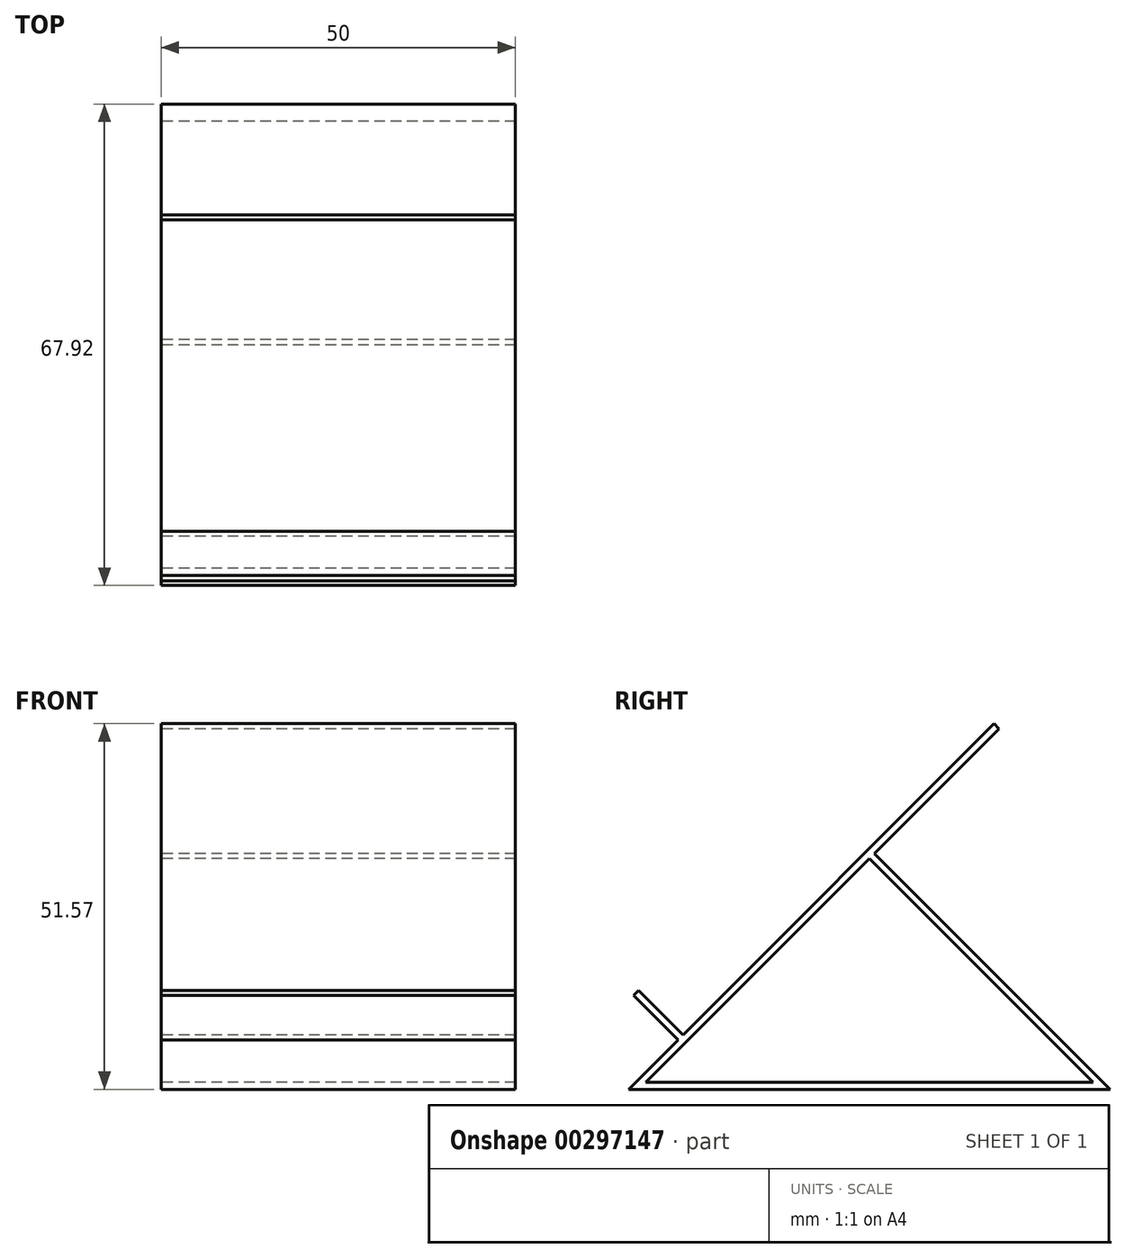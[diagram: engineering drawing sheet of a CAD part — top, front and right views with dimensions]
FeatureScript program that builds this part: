
annotation { "Feature Type Name" : "Feature", "Feature Type Description" : "" }
export const myFeature = defineFeature(function(context is Context, id is Id, definition is map)
    precondition{}
    {
        {
            var Q0;
            Q0=qCreatedBy(makeId("Right.planeOp"),FACE);
            var sketch = newSketch(context, id + "F0", { "sketchPlane" : qUnion([Q0])});
            skLineSegment(sketch, "E0", {"start": v(-32.75, 0) * mm, "end": v(32.75, 0) * mm, "construction": true});
            skLineSegment(sketch, "E1", {"start": v(-32.75, 0) * mm, "end": v(17.97, 50.72) * mm, "construction": true});
            skLineSegment(sketch, "E2", {"start": v(32.75, 0) * mm, "end": v(0, 32.75) * mm, "construction": true});
            skLineSegment(sketch, "E3.0", {"start": v(-33.96, -0.5) * mm, "end": v(-27, 6.46) * mm});
            skLineSegment(sketch, "E4.0", {"start": v(-31.54, 0.5) * mm, "end": v(0, 32.04) * mm});
            skLineSegment(sketch, "E5.0", {"start": v(33.96, -0.5) * mm, "end": v(0.7, 32.75) * mm});
            skLineSegment(sketch, "E6.0", {"start": v(-31.54, 0.5) * mm, "end": v(31.54, 0.5) * mm});
            skLineSegment(sketch, "E7.0", {"start": v(31.54, 0.5) * mm, "end": v(0, 32.04) * mm});
            skLineSegment(sketch, "E8.0", {"start": v(-33.96, -0.5) * mm, "end": v(33.96, -0.5) * mm});
            skLineSegment(sketch, "E9", {"start": v(17.61, 51.07) * mm, "end": v(18.32, 50.37) * mm});
            skLineSegment(sketch, "E10.trimOffspring", {"start": v(0.7, 32.75) * mm, "end": v(18.32, 50.37) * mm});
            skLineSegment(sketch, "E11", {"start": v(-32.92, 13.09) * mm, "end": v(-26.3, 6.46) * mm, "construction": true});
            skLineSegment(sketch, "E12.0", {"start": v(-32.57, 13.44) * mm, "end": v(-26.3, 7.17) * mm});
            skLineSegment(sketch, "E13.0", {"start": v(-33.27, 12.74) * mm, "end": v(-27, 6.46) * mm});
            skLineSegment(sketch, "E14", {"start": v(-32.57, 13.44) * mm, "end": v(-33.27, 12.74) * mm});
            skLineSegment(sketch, "E15.trimOffspring", {"start": v(-26.3, 7.17) * mm, "end": v(17.61, 51.07) * mm});
            skSolve(sketch);
        }
        {
            var Q0;
            Q0=makeQuery(id+"F0.imprint","IMPRINT",FACE,{"disambiguationData":[TD([[makeQuery(id+"F0.imprint","IMPRINT",EDGE,{"derivedFrom":sQuery(id+"F0.wireOp",EDGE,"E3.0")}),-1.0]])]});
            extrude(context, id + "F1", {"entities" : qUnion([Q0]), "endBound" : BoundingType.SYMMETRIC, "depth" : 50 * mm});
        }
    });
